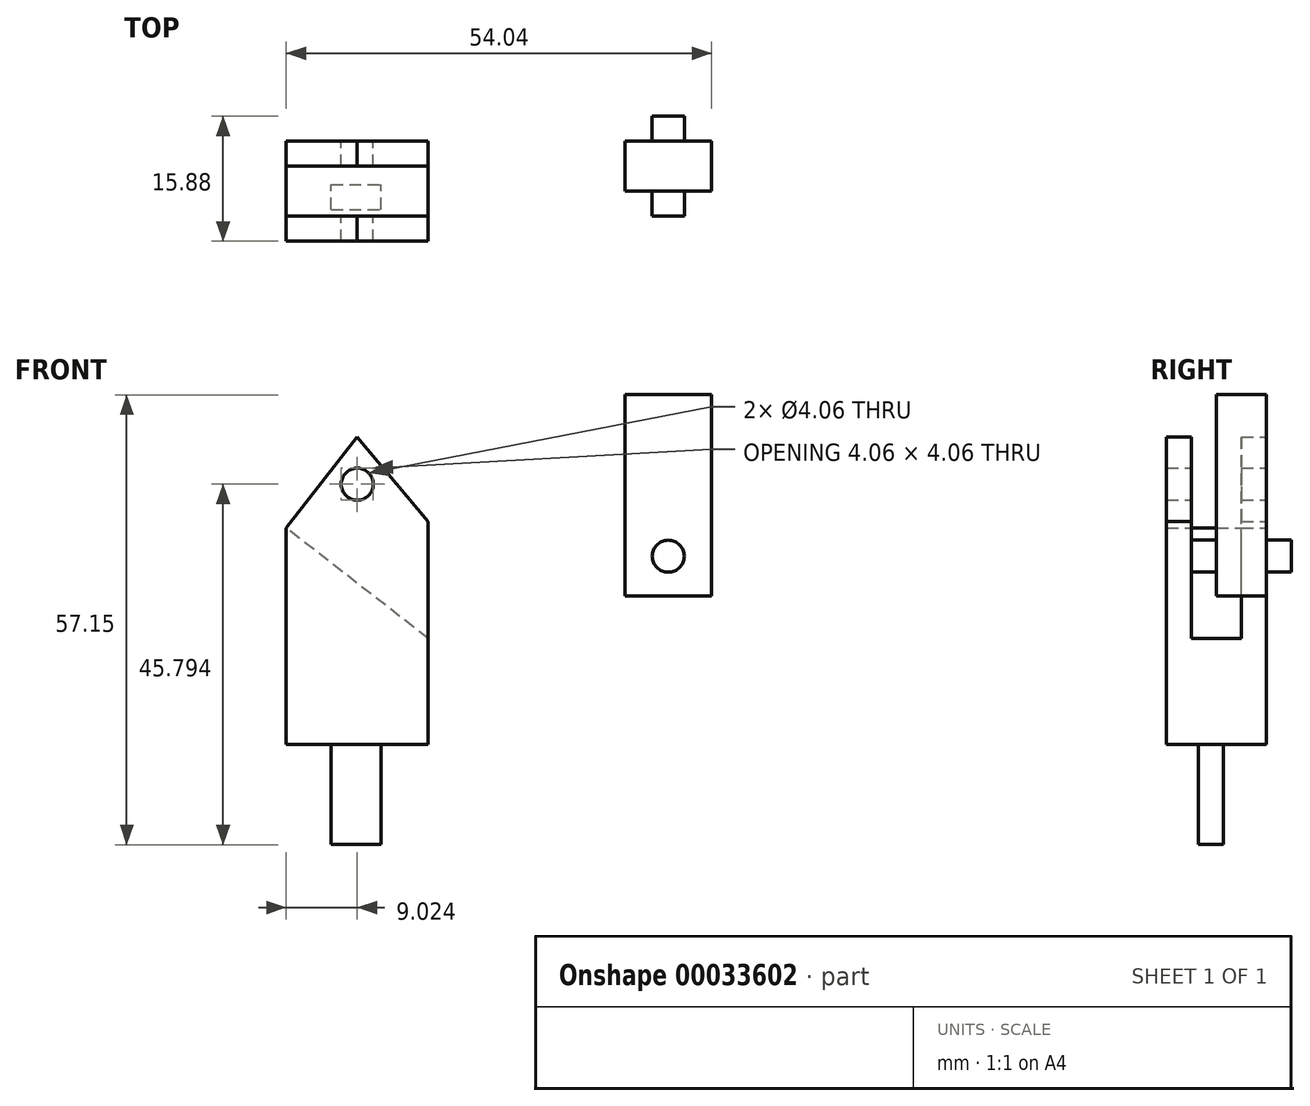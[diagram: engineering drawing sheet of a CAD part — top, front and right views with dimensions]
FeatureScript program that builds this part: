
annotation { "Feature Type Name" : "Feature", "Feature Type Description" : "" }
export const myFeature = defineFeature(function(context is Context, id is Id, definition is map)
    precondition{}
    {
        {
            var Q0;
            Q0=qCreatedBy(makeId("Front.planeOp"),FACE);
            var sketch = newSketch(context, id + "F0", { "sketchPlane" : qUnion([Q0])});
            skLineSegment(sketch, "E0.bottom", {"start": v(-30.45, 36.6) * mm, "end": v(-12.4, 36.6) * mm});
            skLineSegment(sketch, "E0.top", {"start": v(-30.45, -2.52) * mm, "end": v(-12.4, -2.52) * mm});
            skLineSegment(sketch, "E0.left", {"start": v(-30.45, 36.6) * mm, "end": v(-30.45, -2.52) * mm});
            skLineSegment(sketch, "E0.right", {"start": v(-12.4, 36.6) * mm, "end": v(-12.4, -2.52) * mm});
            skLineSegment(sketch, "E1", {"start": v(-21.43, 36.6) * mm, "end": v(-30.45, 25) * mm});
            skLineSegment(sketch, "E2", {"start": v(-21.43, 36.6) * mm, "end": v(-12.4, 25.83) * mm});
            skCircle(sketch, "E3", {"center": v(-21.43, 30.57) * mm, "radius": 2.03 * mm});
            skSolve(sketch);
        }
        {
            var Q0;
            {var subQ3=sQuery(id+"F0.wireOp",EDGE,"E0.top");Q0=makeQuery(id+"F0.imprint","IMPRINT",FACE,{"disambiguationData":[TD([[makeQuery(id+"F0.imprint","IMPRINT",EDGE,{"derivedFrom":subQ3}),1.0]])]});}
            extrude(context, id + "F1", {"entities" : qUnion([Q0]), "depth" : 12.7 * mm});
        }
        {
            var Q0;
            Q0=makeQuery(id+"F1.opExtrude","SWEPT_FACE",FACE,{"disambiguationData":[OSD([sQuery(id+"F0.wireOp",EDGE,"E1")])]});
            var sketch = newSketch(context, id + "F2", { "sketchPlane" : qUnion([Q0])});
            skLineSegment(sketch, "E4.bottom", {"start": v(3.17, 15.73) * mm, "end": v(9.53, 15.73) * mm});
            skLineSegment(sketch, "E4.top", {"start": v(3.17, 1.04) * mm, "end": v(9.53, 1.04) * mm});
            skLineSegment(sketch, "E4.left", {"start": v(3.18, 15.73) * mm, "end": v(3.18, 1.04) * mm});
            skLineSegment(sketch, "E4.right", {"start": v(9.53, 15.73) * mm, "end": v(9.53, 1.04) * mm});
            skPoint(sketch, "E5", {"position": v(0, 15.73) * mm});
            skPoint(sketch, "E6", {"position": v(12.7, 15.73) * mm});
            skLineSegment(sketch, "E7", {"start": v(0, 15.73) * mm, "end": v(3.17, 15.73) * mm});
            skLineSegment(sketch, "E8", {"start": v(9.53, 15.73) * mm, "end": v(12.7, 15.73) * mm});
            skSolve(sketch);
        }
        {
            var Q0;
            Q0 = qSketchRegion(id + "F2", true);
            extrude(context, id + "F3", {"entities" : qUnion([Q0]), "operationType" : NewBodyOperationType.REMOVE, "oppositeDirection" : true, "depth" : 25.4 * mm});
        }
        {
            var Q0;
            Q0=qCreatedBy(makeId("Front.planeOp"),FACE);
            var sketch = newSketch(context, id + "F4", { "sketchPlane" : qUnion([Q0])});
            skLineSegment(sketch, "E9.bottom", {"start": v(12.58, 41.93) * mm, "end": v(23.59, 41.93) * mm});
            skLineSegment(sketch, "E9.top", {"start": v(12.58, 16.34) * mm, "end": v(23.59, 16.34) * mm});
            skLineSegment(sketch, "E9.left", {"start": v(12.58, 41.93) * mm, "end": v(12.58, 16.34) * mm});
            skLineSegment(sketch, "E9.right", {"start": v(23.59, 41.93) * mm, "end": v(23.59, 16.34) * mm});
            skPoint(sketch, "E10.centerSnap0", {"position": v(18.09, 16.34) * mm});
            skSolve(sketch);
        }
        {
            var Q0;
            Q0 = qSketchRegion(id + "F4", true);
            extrude(context, id + "F5", {"entities" : qUnion([Q0]), "depth" : 6.35 * mm});
        }
        {
            var Q0;
            Q0=makeQuery(id+"F5.opExtrude","CAP_FACE",FACE,{"disambiguationData":[OSD([sQuery(id+"F4.wireOp",EDGE,"E9.bottom"),sQuery(id+"F4.wireOp",EDGE,"E9.top"),sQuery(id+"F4.wireOp",EDGE,"E9.left"),sQuery(id+"F4.wireOp",EDGE,"E9.right")])],"isStart":false});
            var sketch = newSketch(context, id + "F6", { "sketchPlane" : qUnion([Q0])});
            skCircle(sketch, "E11", {"center": v(18.09, 21.42) * mm, "radius": 2.03 * mm});
            skPoint(sketch, "E11.centerSnap0", {"position": v(18.09, 16.34) * mm});
            skSolve(sketch);
        }
        {
            var Q0;
            Q0=makeQuery(id+"F5.opExtrude","CAP_FACE",FACE,{"disambiguationData":[OSD([sQuery(id+"F4.wireOp",EDGE,"E9.bottom"),sQuery(id+"F4.wireOp",EDGE,"E9.top"),sQuery(id+"F4.wireOp",EDGE,"E9.left"),sQuery(id+"F4.wireOp",EDGE,"E9.right")])],"isStart":true});
            var sketch = newSketch(context, id + "F7", { "sketchPlane" : qUnion([Q0])});
            skCircle(sketch, "E12", {"center": v(-18.09, 21.42) * mm, "radius": 2.03 * mm});
            skPoint(sketch, "E12.centerSnap0", {"position": v(-18.09, 16.34) * mm});
            skSolve(sketch);
        }
        {
            var Q0;
            Q0 = qSketchRegion(id + "F6", true);
            extrude(context, id + "F8", {"entities" : qUnion([Q0]), "operationType" : NewBodyOperationType.ADD, "depth" : 3.17 * mm});
        }
        {
            var Q0;
            Q0 = qSketchRegion(id + "F7", true);
            extrude(context, id + "F9", {"entities" : qUnion([Q0]), "operationType" : NewBodyOperationType.ADD, "depth" : 3.17 * mm});
        }
        {
            var Q0;
            Q0=makeQuery(id+"F1.opExtrude","SWEPT_FACE",FACE,{"disambiguationData":[OSD([sQuery(id+"F0.wireOp",EDGE,"E0.top")])]});
            var sketch = newSketch(context, id + "F10", { "sketchPlane" : qUnion([Q0])});
            skLineSegment(sketch, "E13.bottom", {"start": v(-24.72, 8.65) * mm, "end": v(-18.37, 8.65) * mm});
            skLineSegment(sketch, "E13.top", {"start": v(-24.72, 5.48) * mm, "end": v(-18.37, 5.48) * mm});
            skLineSegment(sketch, "E13.left", {"start": v(-24.72, 8.65) * mm, "end": v(-24.72, 5.48) * mm});
            skLineSegment(sketch, "E13.right", {"start": v(-18.37, 8.65) * mm, "end": v(-18.37, 5.48) * mm});
            skSolve(sketch);
        }
        {
            var Q0;
            Q0 = qSketchRegion(id + "F10", true);
            extrude(context, id + "F11", {"entities" : qUnion([Q0]), "operationType" : NewBodyOperationType.ADD, "depth" : 12.7 * mm});
        }
    });
